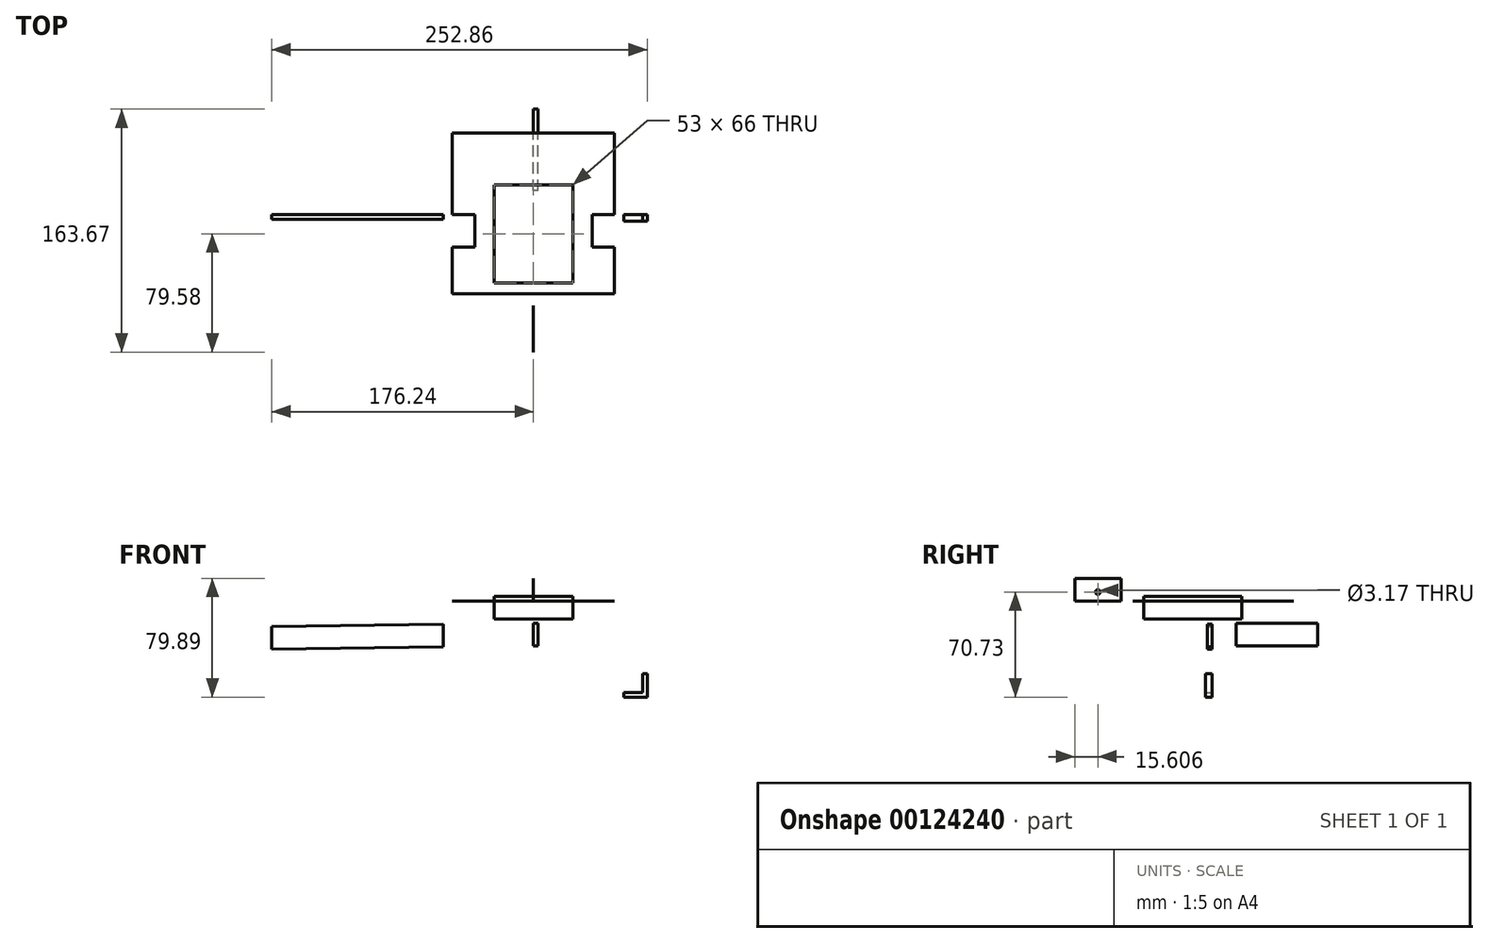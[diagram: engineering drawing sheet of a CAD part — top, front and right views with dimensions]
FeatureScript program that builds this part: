
annotation { "Feature Type Name" : "Feature", "Feature Type Description" : "" }
export const myFeature = defineFeature(function(context is Context, id is Id, definition is map)
    precondition{}
    {
        {
            var Q0;
            Q0=qCreatedBy(makeId("Top.planeOp"),FACE);
            var sketch = newSketch(context, id + "F0", { "sketchPlane" : qUnion([Q0])});
            skLineSegment(sketch, "E0", {"start": v(-54.6, -53.22) * mm, "end": v(54.6, -53.22) * mm});
            skLineSegment(sketch, "E1", {"start": v(-54.6, 0) * mm, "end": v(-39.6, 0) * mm});
            skLineSegment(sketch, "E2", {"start": v(-39.6, 0) * mm, "end": v(-39.6, -22) * mm});
            skLineSegment(sketch, "E3", {"start": v(-39.6, -22) * mm, "end": v(-54.6, -22) * mm});
            skLineSegment(sketch, "E4", {"start": v(-54.6, 0) * mm, "end": v(-54.6, 54.98) * mm});
            skLineSegment(sketch, "E5", {"start": v(-54.6, -22) * mm, "end": v(-54.6, -53.22) * mm});
            skLineSegment(sketch, "E6", {"start": v(54.6, 0) * mm, "end": v(39.6, 0) * mm});
            skLineSegment(sketch, "E7", {"start": v(39.6, 0) * mm, "end": v(39.6, -22) * mm});
            skLineSegment(sketch, "E8", {"start": v(39.6, -22) * mm, "end": v(54.6, -22) * mm});
            skLineSegment(sketch, "E9", {"start": v(54.6, 54.98) * mm, "end": v(54.6, 0) * mm});
            skLineSegment(sketch, "E10", {"start": v(54.6, -22) * mm, "end": v(54.6, -53.22) * mm});
            skLineSegment(sketch, "E11", {"start": v(-54.6, 54.98) * mm, "end": v(54.6, 54.98) * mm});
            skLineSegment(sketch, "E12.bottom", {"start": v(-26.5, -46) * mm, "end": v(26.5, -46) * mm});
            skLineSegment(sketch, "E12.top", {"start": v(-26.5, 20) * mm, "end": v(26.5, 20) * mm});
            skLineSegment(sketch, "E12.left", {"start": v(-26.5, -46) * mm, "end": v(-26.5, 20) * mm});
            skLineSegment(sketch, "E12.right", {"start": v(26.5, -46) * mm, "end": v(26.5, 20) * mm});
            skSolve(sketch);
        }
        {
            var Q0;
            Q0=qCreatedBy(makeId("Right.planeOp"),FACE);
            var sketch = newSketch(context, id + "F1", { "sketchPlane" : qUnion([Q0])});
            skLineSegment(sketch, "E13", {"start": v(-92.58, 0) * mm, "end": v(-92.58, 15.16) * mm});
            skLineSegment(sketch, "E14", {"start": v(-92.58, 15.16) * mm, "end": v(-61.37, 15.16) * mm});
            skLineSegment(sketch, "E15", {"start": v(-61.37, 15.16) * mm, "end": v(-61.37, 0) * mm});
            skLineSegment(sketch, "E16", {"start": v(-61.37, 0) * mm, "end": v(-92.58, 0) * mm});
            skCircle(sketch, "E17", {"center": v(-76.97, 6) * mm, "radius": 1.59 * mm});
            skLineSegment(sketch, "E18", {"start": v(71.09, -30.17) * mm, "end": v(71.09, -15) * mm});
            skLineSegment(sketch, "E19", {"start": v(16.14, -30.17) * mm, "end": v(16.14, -15) * mm});
            skLineSegment(sketch, "E20", {"start": v(16.14, -15) * mm, "end": v(71.09, -15) * mm});
            skLineSegment(sketch, "E21", {"start": v(16.14, -30.17) * mm, "end": v(71.09, -30.17) * mm});
            skSolve(sketch);
        }
        {
            var Q0;
            Q0=qCreatedBy(makeId("Front.planeOp"),FACE);
            var sketch = newSketch(context, id + "F2", { "sketchPlane" : qUnion([Q0])});
            skLineSegment(sketch, "E22", {"start": v(-176.24, -17.2) * mm, "end": v(-176.24, -32.36) * mm});
            skLineSegment(sketch, "E23", {"start": v(-176.24, -17.2) * mm, "end": v(-60.7, -15.6) * mm});
            skLineSegment(sketch, "E24", {"start": v(-60.7, -15.6) * mm, "end": v(-60.7, -30.77) * mm});
            skLineSegment(sketch, "E25", {"start": v(-176.24, -32.36) * mm, "end": v(-60.7, -30.77) * mm});
            skLineSegment(sketch, "E26", {"start": v(73.41, -48.85) * mm, "end": v(73.41, -61.55) * mm});
            skLineSegment(sketch, "E27", {"start": v(73.41, -61.55) * mm, "end": v(60.71, -61.55) * mm});
            skLineSegment(sketch, "E28", {"start": v(60.71, -61.55) * mm, "end": v(60.71, -64.73) * mm});
            skLineSegment(sketch, "E29", {"start": v(60.71, -64.73) * mm, "end": v(76.62, -64.73) * mm});
            skLineSegment(sketch, "E30", {"start": v(73.41, -48.85) * mm, "end": v(76.59, -48.85) * mm});
            skLineSegment(sketch, "E31", {"start": v(76.62, -64.73) * mm, "end": v(76.59, -48.85) * mm});
            skSolve(sketch);
        }
        {
            var Q0;
            Q0=makeQuery(id+"F0.imprint","IMPRINT",FACE,{"disambiguationData":[TD([[makeQuery(id+"F0.imprint","IMPRINT",EDGE,{"derivedFrom":sQuery(id+"F0.wireOp",EDGE,"E0")}),1.0]])]});
            extrude(context, id + "F3", {"entities" : qUnion([Q0]), "depth" : 1 / 203.2 * mm});
        }
        {
            var Q0;
            Q0=makeQuery(id+"F1.imprint","IMPRINT",FACE,{"disambiguationData":[TD([[makeQuery(id+"F1.imprint","IMPRINT",EDGE,{"derivedFrom":sQuery(id+"F1.wireOp",EDGE,"E13")}),-1.0]])]});
            extrude(context, id + "F4", {"entities" : qUnion([Q0]), "operationType" : NewBodyOperationType.ADD, "depth" : 1 / 203.2 * mm});
        }
        {
            var Q0;
            Q0=makeQuery(id+"F1.imprint","IMPRINT",FACE,{"disambiguationData":[TD([[makeQuery(id+"F1.imprint","IMPRINT",EDGE,{"derivedFrom":sQuery(id+"F1.wireOp",EDGE,"E18")}),1.0]])]});
            extrude(context, id + "F5", {"entities" : qUnion([Q0]), "depth" : 3.17 * mm});
        }
        {
            var Q0;
            Q0=makeQuery(id+"F2.imprint","IMPRINT",FACE,{"disambiguationData":[TD([[makeQuery(id+"F2.imprint","IMPRINT",EDGE,{"derivedFrom":sQuery(id+"F2.wireOp",EDGE,"E22")}),1.0]])]});
            extrude(context, id + "F6", {"entities" : qUnion([Q0]), "depth" : 3.17 * mm});
        }
        {
            var Q0;
            Q0=makeQuery(id+"F0.imprint","IMPRINT",FACE,{"disambiguationData":[TD([[makeQuery(id+"F0.imprint","IMPRINT",EDGE,{"derivedFrom":sQuery(id+"F0.wireOp",EDGE,"E12.bottom")}),1.0]])]});
            extrude(context, id + "F7", {"entities" : qUnion([Q0]), "depth" : 3.17 * mm, "hasSecondDirection" : true, "secondDirectionOppositeDirection" : true, "secondDirectionDepth" : 12 * mm});
        }
        {
            var Q0;
            Q0=makeQuery(id+"F2.imprint","IMPRINT",FACE,{"disambiguationData":[TD([[makeQuery(id+"F2.imprint","IMPRINT",EDGE,{"derivedFrom":sQuery(id+"F2.wireOp",EDGE,"E26")}),1.0]])]});
            extrude(context, id + "F8", {"entities" : qUnion([Q0]), "depth" : 4.44 * mm});
        }
    });
